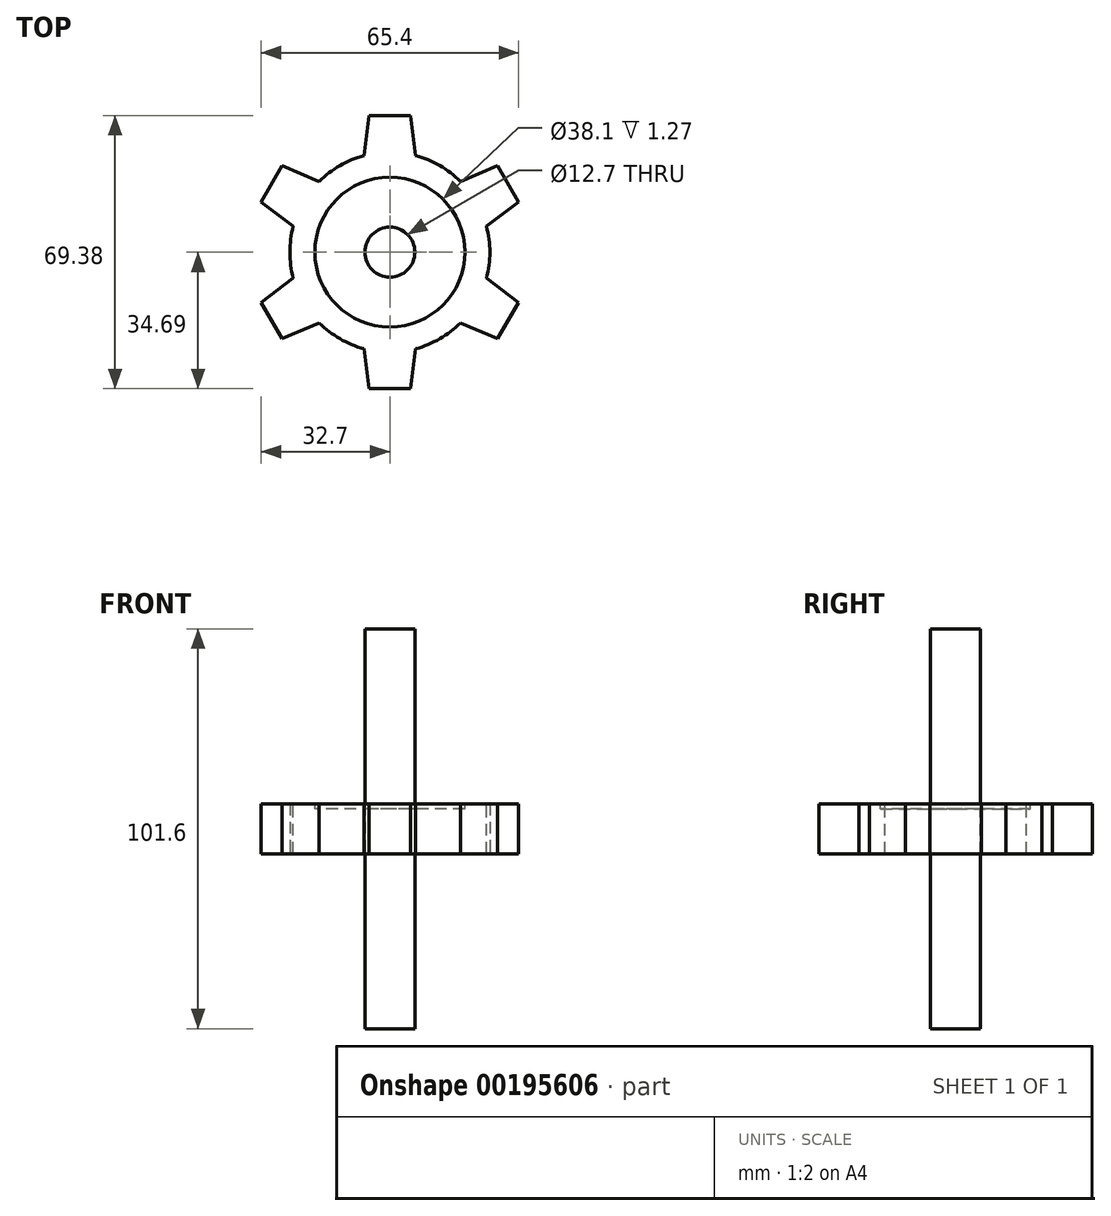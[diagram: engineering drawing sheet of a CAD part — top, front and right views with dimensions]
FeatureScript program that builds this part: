
annotation { "Feature Type Name" : "Feature", "Feature Type Description" : "" }
export const myFeature = defineFeature(function(context is Context, id is Id, definition is map)
    precondition{}
    {
        {
            var Q0;
            Q0=qCreatedBy(makeId("Top.planeOp"),FACE);
            var sketch = newSketch(context, id + "F0", { "sketchPlane" : qUnion([Q0])});
            skCircle(sketch, "E0", {"center": v(0, 0) * mm, "radius": 25.4 * mm});
            skSolve(sketch);
        }
        {
            var Q0;
            Q0 = qSketchRegion(id + "F0", true);
            extrude(context, id + "F1", {"entities" : qUnion([Q0]), "endBound" : BoundingType.SYMMETRIC, "depth" : 12.7 * mm});
        }
        {
            var Q0;
            Q0=makeQuery(id+"F1.opExtrude","CAP_FACE",FACE,{"disambiguationData":[OSD([sQuery(id+"F0.wireOp",EDGE,"E0")])],"isStart":false});
            var sketch = newSketch(context, id + "F2", { "sketchPlane" : qUnion([Q0])});
            skLineSegment(sketch, "E1", {"start": v(0, 0) * mm, "end": v(6.57, 24.53) * mm});
            skLineSegment(sketch, "E2", {"start": v(0, 0) * mm, "end": v(-6.57, 24.53) * mm});
            skLineSegment(sketch, "E3", {"start": v(-6.57, 24.53) * mm, "end": v(6.57, 24.53) * mm});
            skLineSegment(sketch, "E4.0", {"start": v(-6.57, 34.7) * mm, "end": v(6.57, 34.7) * mm});
            skLineSegment(sketch, "E5", {"start": v(-6.57, 24.53) * mm, "end": v(-6.57, 34.7) * mm});
            skLineSegment(sketch, "E6", {"start": v(6.57, 24.53) * mm, "end": v(6.57, 34.7) * mm});
            skSolve(sketch);
        }
        {
            var Q0;
            Q0=makeQuery(id+"F2.imprint","IMPRINT",FACE,{"disambiguationData":[TD([[makeQuery(id+"F2.imprint","IMPRINT",EDGE,{"derivedFrom":sQuery(id+"F2.wireOp",EDGE,"E4.0")}),-1.0]])]});
            extrude(context, id + "F3", {"entities" : qUnion([Q0]), "operationType" : NewBodyOperationType.ADD, "oppositeDirection" : true, "depth" : 12.7 * mm});
        }
        {
            var Q0;
            Q0=makeQuery(id+"F3.opExtrude","SWEPT_EDGE",EDGE,{"disambiguationData":[OSD([sQuery(id+"F2.wireOp",EDGE,"E4.0"),sQuery(id+"F2.wireOp",EDGE,"E6")])]});
            var Q1;
            Q1=makeQuery(id+"F3.opExtrude","SWEPT_EDGE",EDGE,{"disambiguationData":[OSD([sQuery(id+"F2.wireOp",EDGE,"E4.0"),sQuery(id+"F2.wireOp",EDGE,"E5")])]});
            chamfer(context, id + "F4", {"entities" : qUnion([Q0, Q1]), "chamferType" : ChamferType.TWO_OFFSETS, "width1" : 10.16 * mm, "oppositeDirection" : false, "width2" : 1.27 * mm, "tangentPropagation" : true});
        }
        {
            var Q0;
            Q0=qCreatedBy(makeId("Front.planeOp"),FACE);
            var sketch = newSketch(context, id + "F5", { "sketchPlane" : qUnion([Q0])});
            skLineSegment(sketch, "E7", {"start": v(0, 0) * mm, "end": v(0, 44) * mm});
            skSolve(sketch);
        }
        {
            var Q0;
            Q0=makeQuery(id+"F1.opExtrude","SWEPT_BODY",BODY,{"disambiguationData":[OSD([sQuery(id+"F0.wireOp",EDGE,"E0")])]});
            var Q1;
            Q1=sQuery(id+"F5.wireOp",EDGE,"E7");
            circularPattern(context, id + "F6", {"operationType" : NewBodyOperationType.ADD, "entities" : qUnion([Q0]), "axis" : qUnion([Q1]), "angle" : 360 * degree, "instanceCount" : 6, "equalSpace" : true});
        }
        {
            var Q0;
            {var subQ0=sQuery(id+"F0.wireOp",EDGE,"E0");var subQ1=makeQuery(id+"F3.boolean.opBoolean","MERGE",FACE,{"derivedFrom":[makeQuery(id+"F1.opExtrude","CAP_FACE",FACE,{"disambiguationData":[OSD([subQ0])],"isStart":false}),makeQuery(id+"F3.opExtrude","CAP_FACE",FACE,{"disambiguationData":[OSD([subQ0,sQuery(id+"F2.wireOp",EDGE,"E4.0"),sQuery(id+"F2.wireOp",EDGE,"E5"),sQuery(id+"F2.wireOp",EDGE,"E6")])],"isStart":true})]});Q0=makeQuery(id+"F6.boolean.opBoolean","MERGE",FACE,{"derivedFrom":[subQ1,makeQuery(id+"F6.opPattern","COPY",FACE,{"derivedFrom":subQ1,"instanceName":"1"}),makeQuery(id+"F6.opPattern","COPY",FACE,{"derivedFrom":subQ1,"instanceName":"2"}),makeQuery(id+"F6.opPattern","COPY",FACE,{"derivedFrom":subQ1,"instanceName":"3"}),makeQuery(id+"F6.opPattern","COPY",FACE,{"derivedFrom":subQ1,"instanceName":"4"}),makeQuery(id+"F6.opPattern","COPY",FACE,{"derivedFrom":subQ1,"instanceName":"5"})]});}
            var sketch = newSketch(context, id + "F7", { "sketchPlane" : qUnion([Q0])});
            skCircle(sketch, "E8", {"center": v(0, 0) * mm, "radius": 19.05 * mm});
            skPoint(sketch, "E9.center.orphan", {"position": v(0, -1.5) * mm});
            skCircle(sketch, "E10", {"center": v(0, 0) * mm, "radius": 6.35 * mm});
            skSolve(sketch);
        }
        {
            var Q0;
            Q0 = qSketchRegion(id + "F7", true);
            var Q1;
            Q1=makeQuery(id+"F7.imprint","IMPRINT",FACE,{"disambiguationData":[TD([[makeQuery(id+"F7.imprint","IMPRINT",EDGE,{"derivedFrom":sQuery(id+"F7.wireOp",EDGE,"E10")}),1.0]])]});
            extrude(context, id + "F8", {"entities" : qUnion([Q0, Q1]), "operationType" : NewBodyOperationType.REMOVE, "oppositeDirection" : true, "depth" : 1.27 * mm});
        }
        {
            var Q0;
            Q0=makeQuery(id+"F7.imprint","IMPRINT",FACE,{"disambiguationData":[TD([[makeQuery(id+"F7.imprint","IMPRINT",EDGE,{"derivedFrom":sQuery(id+"F7.wireOp",EDGE,"E10")}),1.0]])]});
            extrude(context, id + "F9", {"entities" : qUnion([Q0]), "operationType" : NewBodyOperationType.REMOVE, "oppositeDirection" : true, "depth" : 25.4 * mm});
        }
        {
            var Q0;
            Q0=qCreatedBy(makeId("Top.planeOp"),FACE);
            var sketch = newSketch(context, id + "F10", { "sketchPlane" : qUnion([Q0])});
            skCircle(sketch, "E11", {"center": v(0, 0) * mm, "radius": 6.35 * mm});
            skSolve(sketch);
        }
        {
            var Q0;
            Q0 = qSketchRegion(id + "F10", true);
            extrude(context, id + "F11", {"entities" : qUnion([Q0]), "endBound" : BoundingType.SYMMETRIC, "depth" : 101.6 * mm});
        }
    });
